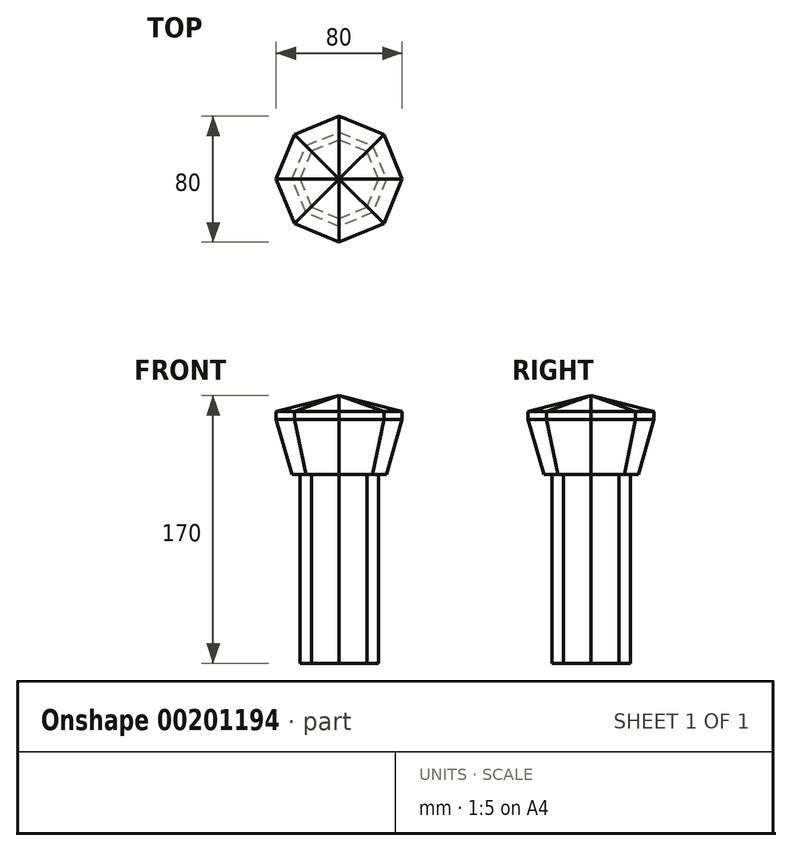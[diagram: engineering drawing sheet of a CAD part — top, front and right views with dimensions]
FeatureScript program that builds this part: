
annotation { "Feature Type Name" : "Feature", "Feature Type Description" : "" }
export const myFeature = defineFeature(function(context is Context, id is Id, definition is map)
    precondition{}
    {
        {
            var Q0;
            Q0=qCreatedBy(makeId("Front.planeOp"),FACE);
            var sketch = newSketch(context, id + "F0", { "sketchPlane" : qUnion([Q0])});
            skLineSegment(sketch, "E0", {"start": v(0, 0) * mm, "end": v(25, 0) * mm});
            skLineSegment(sketch, "E1", {"start": v(25, 0) * mm, "end": v(25, 120) * mm});
            skLineSegment(sketch, "E2", {"start": v(25, 120) * mm, "end": v(30, 120) * mm});
            skLineSegment(sketch, "E3", {"start": v(30, 120) * mm, "end": v(40, 155) * mm});
            skLineSegment(sketch, "E4", {"start": v(40, 155) * mm, "end": v(40, 160) * mm});
            skLineSegment(sketch, "E5", {"start": v(40, 160) * mm, "end": v(0, 170) * mm});
            skLineSegment(sketch, "E6", {"start": v(0, 170) * mm, "end": v(0, 0) * mm});
            skSolve(sketch);
        }
        {
            var Q0;
            Q0=qCreatedBy(makeId("Front.planeOp"),FACE);
            var Q1;
            Q1=sQuery(id+"F0.wireOp",EDGE,"E6");
            cPlane(context, id + "F1", {"entities" : qUnion([Q0, Q1]), "cplaneType" : CPlaneType.LINE_ANGLE, "offset" : 25 * mm, "angle" : 135 * degree, "width" : 150 * mm, "height" : 150 * mm});
        }
        {
            var Q0;
            Q0=qCreatedBy(id+"F1.planeOp",FACE);
            var sketch = newSketch(context, id + "F2", { "sketchPlane" : qUnion([Q0])});
            skLineSegment(sketch, "E7", {"start": v(0, 0) * mm, "end": v(25, 0) * mm});
            skLineSegment(sketch, "E8", {"start": v(25, 0) * mm, "end": v(25, 120) * mm});
            skLineSegment(sketch, "E9", {"start": v(25, 120) * mm, "end": v(30, 120) * mm});
            skLineSegment(sketch, "E10", {"start": v(30, 120) * mm, "end": v(40, 155) * mm});
            skLineSegment(sketch, "E11", {"start": v(40, 155) * mm, "end": v(40, 160) * mm});
            skLineSegment(sketch, "E12", {"start": v(40, 160) * mm, "end": v(0, 170) * mm});
            skLineSegment(sketch, "E13", {"start": v(0, 170) * mm, "end": v(0, 0) * mm});
            skSolve(sketch);
        }
        {
            var Q0;
            Q0=qCreatedBy(makeId("Top.planeOp"),FACE);
            var sketch = newSketch(context, id + "F3", { "sketchPlane" : qUnion([Q0])});
            skLineSegment(sketch, "E14", {"start": v(25, 0) * mm, "end": v(17.68, 17.68) * mm});
            skSolve(sketch);
        }
        {
            var Q0;
            Q0=makeQuery(id+"F2.imprint","IMPRINT",FACE,{"disambiguationData":[TD([[makeQuery(id+"F2.imprint","IMPRINT",EDGE,{"derivedFrom":sQuery(id+"F2.wireOp",EDGE,"E7")}),1.0]])]});
            var Q1;
            Q1=makeQuery(id+"F0.imprint","IMPRINT",FACE,{"disambiguationData":[TD([[makeQuery(id+"F0.imprint","IMPRINT",EDGE,{"derivedFrom":sQuery(id+"F0.wireOp",EDGE,"E0")}),1.0]])]});
            var Q2;
            Q2=sQuery(id+"F3.wireOp",EDGE,"E14");
            loft(context, id + "F4", {"addGuides" : true, "sheetProfilesArray" : [{ "sheetProfileEntities" : qUnion([Q0]) }, { "sheetProfileEntities" : qUnion([Q1]) }], "guidesArray" : [{ "guideEntities" : qUnion([Q2]), "guideDerivativeType" : LoftGuideDerivativeType.DEFAULT, "guideDerivativeMagnitude" : 1 }]});
        }
        {
            var Q0;
            Q0=makeQuery(id+"F4.opLoft","SWEPT_BODY",BODY,{"disambiguationData":[OSD([makeQuery(id+"F0.imprint","IMPRINT",FACE,{"disambiguationData":[TD([[makeQuery(id+"F0.imprint","IMPRINT",EDGE,{"derivedFrom":sQuery(id+"F0.wireOp",EDGE,"E0")}),1.0]])]}),makeQuery(id+"F2.imprint","IMPRINT",FACE,{"disambiguationData":[TD([[makeQuery(id+"F2.imprint","IMPRINT",EDGE,{"derivedFrom":sQuery(id+"F2.wireOp",EDGE,"E7")}),1.0]])]}),sQuery(id+"F3.wireOp",EDGE,"E14")])]});
            var Q1;
            Q1=makeQuery(id+"F4.opLoft","CAP_EDGE",EDGE,{"disambiguationData":[OSD([sQuery(id+"F0.wireOp",EDGE,"E6"),sQuery(id+"F2.wireOp",EDGE,"E13")])],"isStart":false});
            circularPattern(context, id + "F5", {"entities" : qUnion([Q0]), "axis" : qUnion([Q1]), "angle" : 360 * degree, "instanceCount" : 8, "oppositeDirection" : true, "equalSpace" : true});
        }
    });
